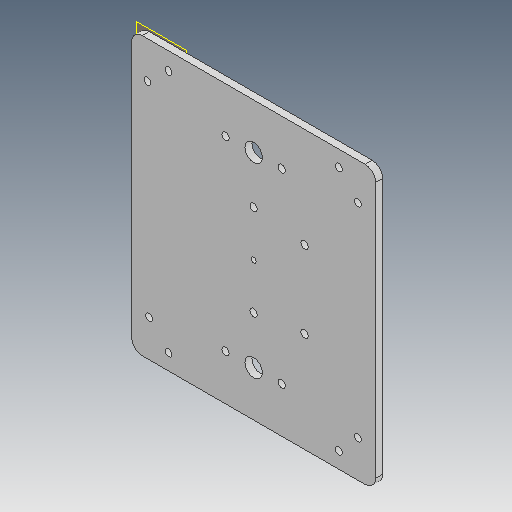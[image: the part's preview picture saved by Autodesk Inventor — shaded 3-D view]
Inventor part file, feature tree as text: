
AUTODESK INVENTOR PART (.ipt)
format: ipt  version: 2020 (Build 240168000, 168)  size: 174,592 bytes
history: native  units: mm
features: other x23, extrude x4, sketch x4
ambient origin geometry x8: Origin, YZ Plane, XZ Plane, XY Plane, X Axis, Y Axis, Z Axis, Center Point
bodies: Body1 (feature_tree)
feature tree (31):
  other  "Sólido1"
  other  "Plano de trabalho1"
  extrude  "Extrusão1"  Depth=10.0mm
  extrude  "Extrusão2"  Depth=3.0mm
  extrude  "Extrusão3"  Depth=4.0mm
  extrude  "Extrusão4"  Depth=4.0mm
  sketch  "Esboço1"  dims[d0=4.0mm d1=0.0mm d2=10.0mm]
  other  "Referência1"
  other  "Referência2"
  other  "Referência3"
  other  "Referência4"
  sketch  "Esboço2"  dims[d3=4.2mm d4=3.0mm]
  other  "Referência5"
  other  "Referência6"
  other  "Referência7"
  other  "Referência8"
  other  "Referência9"
  sketch  "Esboço3"  dims[d5=4.0mm d6=0.0mm d7=32.0mm]
  sketch  "Esboço4"  dims[d8=32.0mm d9=4.2mm d10=4.2mm d11=4.2mm d12=4.2mm d13=4.0mm d14=0.0mm d15=4.2mm d16=4.2mm d17=4.0mm d18=0.0mm]
  other  "<userpath>\OneDrive\Área de Trabalho\Calorimetro 2022\Inventor\Calorímetro.iam"
  other  "Calorímetro.iam"
  other  "suporte_fechamento:1"
  other  "suporte_fechamento:2"
  other  "suporte_fechamento2:2"
  other  "suporte_fechamento2:3"
  other  "parte_superior:1"
  other  "guia_10mm:1"
  other  "guia_10mm:2"
  other  "Montagem_corpo_menor:1"
  other  "corpo_1_menor:4"
  other  "Inferior_encaixe:1"
